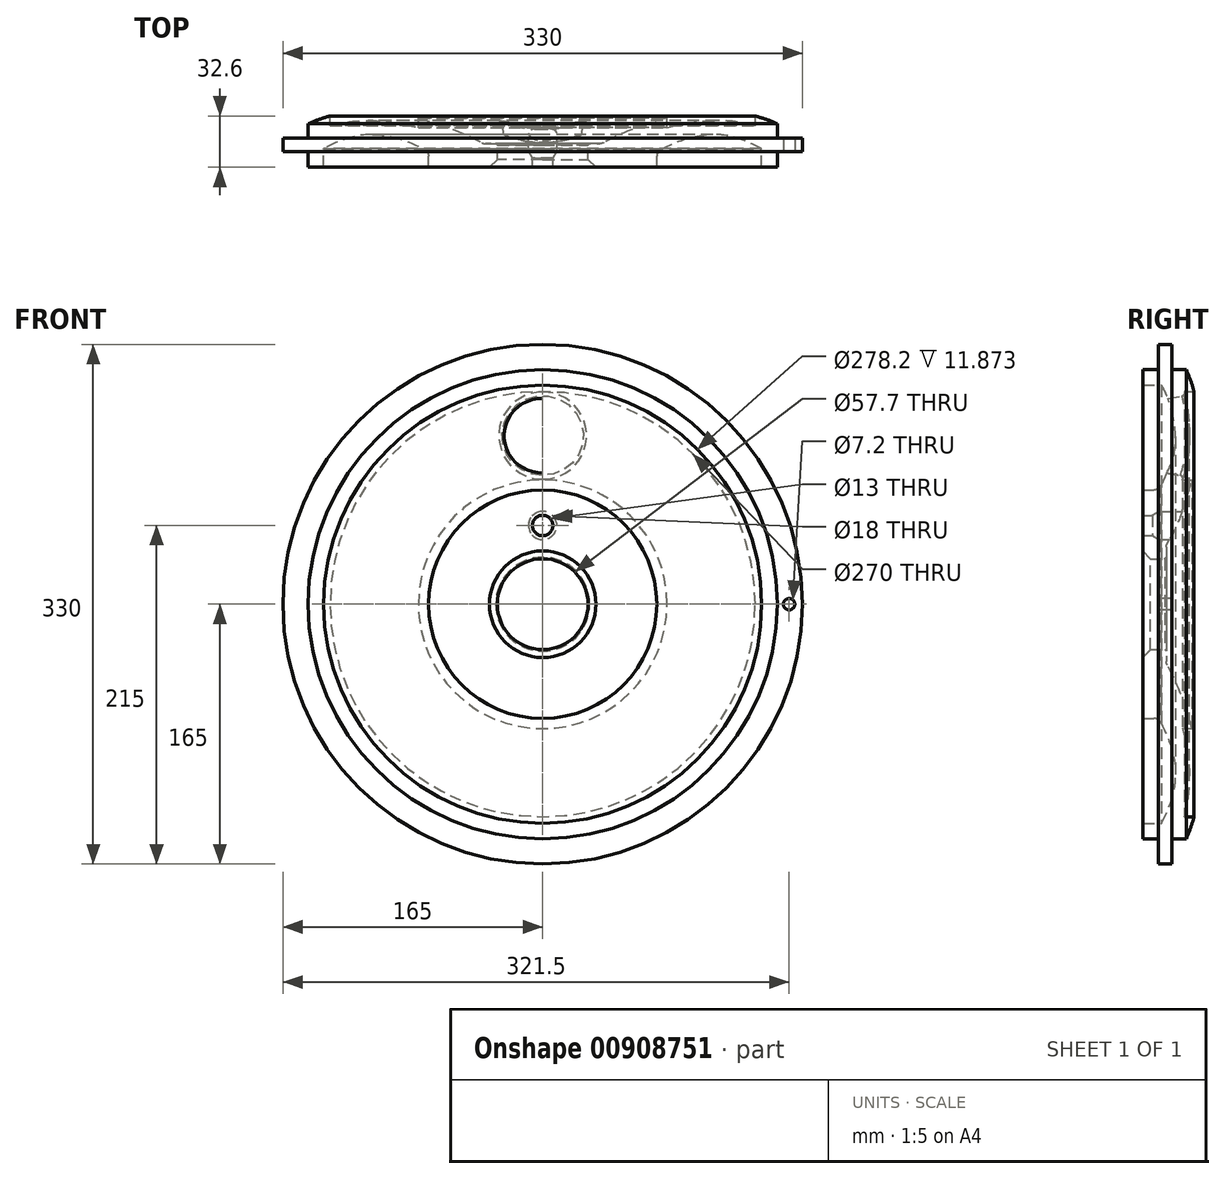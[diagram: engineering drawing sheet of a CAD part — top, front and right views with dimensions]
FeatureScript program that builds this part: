
annotation { "Feature Type Name" : "Feature", "Feature Type Description" : "" }
export const myFeature = defineFeature(function(context is Context, id is Id, definition is map)
    precondition{}
    {
        {
            var Q0;
            Q0=qCreatedBy(makeId("Top.planeOp"),FACE);
            var sketch = newSketch(context, id + "F0", { "sketchPlane" : qUnion([Q0])});
            skLineSegment(sketch, "E0", {"start": v(-28.85, 0) * mm, "end": v(-28.85, 15) * mm});
            skLineSegment(sketch, "E1", {"start": v(-28.85, 15) * mm, "end": v(-36.25, 15) * mm});
            skFitSpline(sketch, "E2", {"points": [v(-37.5, 15) * mm, v(-69.56, 28.6) * mm, v(-105.66, 35.55) * mm, v(-165, 18.67) * mm], "startDerivative": vector(-135.79, 72.9) * mm, "endDerivative": vector(-162.08, -109.99) * mm});
            skLineSegment(sketch, "E3", {"start": v(-165, 10) * mm, "end": v(-149, 10) * mm});
            skLineSegment(sketch, "E4", {"start": v(-149, 10) * mm, "end": v(-149, 0) * mm});
            skLineSegment(sketch, "E5", {"start": v(-149, 0) * mm, "end": v(-139.1, 0) * mm});
            skLineSegment(sketch, "E6", {"start": v(-139.1, 0) * mm, "end": v(-139.1, 11.87) * mm});
            skLineSegment(sketch, "E7", {"start": v(-72.5, 7) * mm, "end": v(-72.5, 0) * mm});
            skLineSegment(sketch, "E8", {"start": v(-72.5, 0) * mm, "end": v(-28.85, 0) * mm});
            skLineSegment(sketch, "E9", {"start": v(0, 47.35) * mm, "end": v(0, -31.33) * mm, "construction": true});
            skFitSpline(sketch, "E10", {"points": [v(-139.1, 11.87) * mm, v(-72.5, 10) * mm], "startDerivative": vector(71.54, 38.93) * mm, "endDerivative": vector(74.78, -40.54) * mm});
            skLineSegment(sketch, "E11", {"start": v(-165, 18.67) * mm, "end": v(-149, 18.67) * mm});
            skLineSegment(sketch, "E12", {"start": v(-149, 18.67) * mm, "end": v(-149, 27.64) * mm});
            skLineSegment(sketch, "E13", {"start": v(-165, 18.67) * mm, "end": v(-165, 10) * mm});
            skArc(sketch, "E14.filletArc", {"start": v(-72.5, 7) * mm, "mid": v(-73.23, 9.6) * mm, "end": v(-75.2, 11.43) * mm});
            skArc(sketch, "E15.filletArc", {"start": v(-38.6, 15.58) * mm, "mid": v(-37.46, 15.15) * mm, "end": v(-36.25, 15) * mm});
            skSolve(sketch);
        }
        {
            var Q0;
            Q0=makeQuery(id+"F0.imprint","IMPRINT",FACE,{"disambiguationData":[TD([[makeQuery(id+"F0.imprint","IMPRINT",EDGE,{"derivedFrom":sQuery(id+"F0.wireOp",EDGE,"E0")}),1.0]])]});
            var Q1;
            Q1=sQuery(id+"F0.wireOp",EDGE,"E9");
            revolve(context, id + "F1", {"surfaceOperationType" : NewSurfaceOperationType.NEW, "entities" : qUnion([Q0]), "axis" : qUnion([Q1]), "revolveType" : RevolveType.FULL});
        }
        {
            var Q0;
            Q0=qCreatedBy(makeId("Front.planeOp"),FACE);
            cPlane(context, id + "F2", {"entities" : qUnion([Q0]), "cplaneType" : CPlaneType.OFFSET, "offset" : 40 * mm, "oppositeDirection" : true, "width" : 150 * mm, "height" : 150 * mm});
        }
        {
            var Q0;
            Q0=qCreatedBy(id+"F2.planeOp",FACE);
            var sketch = newSketch(context, id + "F3", { "sketchPlane" : qUnion([Q0])});
            skPoint(sketch, "E16.visualSharp", {"position": v(0, 43.2) * mm});
            skLineSegment(sketch, "E17", {"start": v(0, 0) * mm, "end": v(0, 148.36) * mm, "construction": true});
            skCircle(sketch, "E18", {"center": v(0, 107) * mm, "radius": 28 * mm});
            skSolve(sketch);
        }
        {
            var Q0;
            Q0=qCreatedBy(makeId("Front.planeOp"),FACE);
            var sketch = newSketch(context, id + "F4", { "sketchPlane" : qUnion([Q0])});
            skCircle(sketch, "E19", {"center": v(156.5, 0) * mm, "radius": 3.6 * mm});
            skSolve(sketch);
        }
        {
            var Q0;
            Q0=qSketchRegion(id+"F4",true);
            extrude(context, id + "F5", {"entities" : qUnion([Q0]), "operationType" : NewBodyOperationType.REMOVE, "oppositeDirection" : true, "depth" : 50 * mm, "offsetDistance" : 25 * mm});
        }
        {
            var Q0;
            Q0=qCreatedBy(makeId("Right.planeOp"),FACE);
            var sketch = newSketch(context, id + "F6", { "sketchPlane" : qUnion([Q0])});
            skLineSegment(sketch, "E20", {"start": v(0, 50) * mm, "end": v(51.06, 50) * mm});
            skLineSegment(sketch, "E21", {"start": v(0, 56.5) * mm, "end": v(6, 56.5) * mm});
            skLineSegment(sketch, "E22", {"start": v(6, 56.5) * mm, "end": v(10.33, 59) * mm});
            skLineSegment(sketch, "E23", {"start": v(10.33, 59) * mm, "end": v(51.06, 59) * mm});
            skLineSegment(sketch, "E24", {"start": v(51.06, 59) * mm, "end": v(51.06, 50) * mm});
            skLineSegment(sketch, "E25", {"start": v(0, 50) * mm, "end": v(0, 56.5) * mm});
            skSolve(sketch);
        }
        {
            var Q0;
            Q0=qSketchRegion(id+"F6",true);
            var Q1;
            Q1=sQuery(id+"F6.wireOp",EDGE,"E20");
            revolve(context, id + "F7", {"operationType" : NewBodyOperationType.REMOVE, "surfaceOperationType" : NewSurfaceOperationType.NEW, "entities" : qUnion([Q0]), "axis" : qUnion([Q1]), "revolveType" : RevolveType.FULL, "oppositeDirection" : true});
        }
        {
            var Q0;
            Q0=makeQuery(id+"F1.opRevolve","SWEPT_EDGE",EDGE,{"disambiguationData":[OSD([sQuery(id+"F0.wireOp",EDGE,"E0"),sQuery(id+"F0.wireOp",EDGE,"E8")])]});
            chamfer(context, id + "F8", {"entities" : qUnion([Q0]), "width" : 5 * mm, "tangentPropagation" : true});
        }
        {
            var Q0;
            Q0=makeQuery(id+"F1.opRevolve","SWEPT_EDGE",EDGE,{"disambiguationData":[OSD([sQuery(id+"F0.wireOp",EDGE,"E0"),sQuery(id+"F0.wireOp",EDGE,"E1")])]});
            chamfer(context, id + "F9", {"entities" : qUnion([Q0]), "width" : 1 * mm, "tangentPropagation" : true});
        }
        {
            var Q0;
            Q0=qSketchRegion(id+"F3",true);
            extrude(context, id + "F10", {"entities" : qUnion([Q0]), "operationType" : NewBodyOperationType.REMOVE, "depth" : 50 * mm, "offsetDistance" : 25 * mm, "hasDraft" : true, "draftAngle" : 10 * degree, "draftPullDirection" : true});
        }
        {
            var Q0;
            Q0=qCreatedBy(id+"F2.planeOp",FACE);
            var sketch = newSketch(context, id + "F11", { "sketchPlane" : qUnion([Q0])});
            skCircle(sketch, "E26", {"center": v(0, 0) * mm, "radius": 135 * mm});
            skCircle(sketch, "E27", {"center": v(0, 0) * mm, "radius": 79 * mm});
            skSolve(sketch);
        }
        {
            var Q0;
            Q0 = qSketchRegion(id + "F11", true);
            var Q1;
            Q1=makeQuery(id+"F1.opRevolve","SWEPT_FACE",FACE,{"disambiguationData":[OSD([sQuery(id+"F0.wireOp",EDGE,"E2")])]});
            extrude(context, id + "F12", {"entities" : qUnion([Q0]), "operationType" : NewBodyOperationType.REMOVE, "endBound" : BoundingType.UP_TO_SURFACE, "depth" : 25 * mm, "endBoundEntityFace" : qUnion([Q1]), "hasOffset" : true, "offsetDistance" : 6 * mm, "offsetOppositeDirection" : true});
        }
        {
            var Q0;
            Q0=makeQuery(id+"F12.boolean.opBoolean","INTERSECT",EDGE,{"derivedFrom":[makeQuery(id+"F10.boolean.opBoolean","COPY",FACE,{"derivedFrom":makeQuery(id+"F10.opExtrude","SWEPT_FACE",FACE,{"disambiguationData":[OSD([sQuery(id+"F3.wireOp",EDGE,"E18")])]})}),makeQuery(id+"F12.opExtrude","CAP_FACE",FACE,{"disambiguationData":[OSD([sQuery(id+"F11.wireOp",EDGE,"E26"),sQuery(id+"F11.wireOp",EDGE,"E27")])],"isStart":false})]});
            var Q1;
            Q1=makeQuery(id+"F12.boolean.opBoolean","INTERSECT",EDGE,{"derivedFrom":[makeQuery(id+"FRi57XyZZzTpHfL_1.11.F10.boolean.opBoolean","COPY",FACE,{"derivedFrom":makeQuery(id+"FRi57XyZZzTpHfL_1.11.F10.opExtrude","SWEPT_FACE",FACE,{"disambiguationData":[OSD([sQuery(id+"F3.wireOp",EDGE,"E18")])]})}),makeQuery(id+"F12.opExtrude","CAP_FACE",FACE,{"disambiguationData":[OSD([sQuery(id+"F11.wireOp",EDGE,"E26"),sQuery(id+"F11.wireOp",EDGE,"E27")])],"isStart":false})]});
            var Q2;
            Q2=makeQuery(id+"F12.boolean.opBoolean","INTERSECT",EDGE,{"derivedFrom":[makeQuery(id+"FRi57XyZZzTpHfL_1.10.F10.boolean.opBoolean","COPY",FACE,{"derivedFrom":makeQuery(id+"FRi57XyZZzTpHfL_1.10.F10.opExtrude","SWEPT_FACE",FACE,{"disambiguationData":[OSD([sQuery(id+"F3.wireOp",EDGE,"E18")])]})}),makeQuery(id+"F12.opExtrude","CAP_FACE",FACE,{"disambiguationData":[OSD([sQuery(id+"F11.wireOp",EDGE,"E26"),sQuery(id+"F11.wireOp",EDGE,"E27")])],"isStart":false})]});
            var Q3;
            Q3=makeQuery(id+"F12.boolean.opBoolean","INTERSECT",EDGE,{"derivedFrom":[makeQuery(id+"FRi57XyZZzTpHfL_1.1.F10.boolean.opBoolean","COPY",FACE,{"derivedFrom":makeQuery(id+"FRi57XyZZzTpHfL_1.1.F10.opExtrude","SWEPT_FACE",FACE,{"disambiguationData":[OSD([sQuery(id+"F3.wireOp",EDGE,"E18")])]})}),makeQuery(id+"F12.opExtrude","CAP_FACE",FACE,{"disambiguationData":[OSD([sQuery(id+"F11.wireOp",EDGE,"E26"),sQuery(id+"F11.wireOp",EDGE,"E27")])],"isStart":false})]});
            var Q4;
            Q4=makeQuery(id+"F12.boolean.opBoolean","INTERSECT",EDGE,{"derivedFrom":[makeQuery(id+"FRi57XyZZzTpHfL_1.2.F10.boolean.opBoolean","COPY",FACE,{"derivedFrom":makeQuery(id+"FRi57XyZZzTpHfL_1.2.F10.opExtrude","SWEPT_FACE",FACE,{"disambiguationData":[OSD([sQuery(id+"F3.wireOp",EDGE,"E18")])]})}),makeQuery(id+"F12.opExtrude","CAP_FACE",FACE,{"disambiguationData":[OSD([sQuery(id+"F11.wireOp",EDGE,"E26"),sQuery(id+"F11.wireOp",EDGE,"E27")])],"isStart":false})]});
            var Q5;
            Q5=makeQuery(id+"F12.boolean.opBoolean","INTERSECT",EDGE,{"derivedFrom":[makeQuery(id+"FRi57XyZZzTpHfL_1.3.F10.boolean.opBoolean","COPY",FACE,{"derivedFrom":makeQuery(id+"FRi57XyZZzTpHfL_1.3.F10.opExtrude","SWEPT_FACE",FACE,{"disambiguationData":[OSD([sQuery(id+"F3.wireOp",EDGE,"E18")])]})}),makeQuery(id+"F12.opExtrude","CAP_FACE",FACE,{"disambiguationData":[OSD([sQuery(id+"F11.wireOp",EDGE,"E26"),sQuery(id+"F11.wireOp",EDGE,"E27")])],"isStart":false})]});
            var Q6;
            Q6=makeQuery(id+"F12.boolean.opBoolean","INTERSECT",EDGE,{"derivedFrom":[makeQuery(id+"FRi57XyZZzTpHfL_1.4.F10.boolean.opBoolean","COPY",FACE,{"derivedFrom":makeQuery(id+"FRi57XyZZzTpHfL_1.4.F10.opExtrude","SWEPT_FACE",FACE,{"disambiguationData":[OSD([sQuery(id+"F3.wireOp",EDGE,"E18")])]})}),makeQuery(id+"F12.opExtrude","CAP_FACE",FACE,{"disambiguationData":[OSD([sQuery(id+"F11.wireOp",EDGE,"E26"),sQuery(id+"F11.wireOp",EDGE,"E27")])],"isStart":false})]});
            var Q7;
            Q7=makeQuery(id+"F12.boolean.opBoolean","INTERSECT",EDGE,{"derivedFrom":[makeQuery(id+"FRi57XyZZzTpHfL_1.5.F10.boolean.opBoolean","COPY",FACE,{"derivedFrom":makeQuery(id+"FRi57XyZZzTpHfL_1.5.F10.opExtrude","SWEPT_FACE",FACE,{"disambiguationData":[OSD([sQuery(id+"F3.wireOp",EDGE,"E18")])]})}),makeQuery(id+"F12.opExtrude","CAP_FACE",FACE,{"disambiguationData":[OSD([sQuery(id+"F11.wireOp",EDGE,"E26"),sQuery(id+"F11.wireOp",EDGE,"E27")])],"isStart":false})]});
            var Q8;
            Q8=makeQuery(id+"F12.boolean.opBoolean","INTERSECT",EDGE,{"derivedFrom":[makeQuery(id+"FRi57XyZZzTpHfL_1.6.F10.boolean.opBoolean","COPY",FACE,{"derivedFrom":makeQuery(id+"FRi57XyZZzTpHfL_1.6.F10.opExtrude","SWEPT_FACE",FACE,{"disambiguationData":[OSD([sQuery(id+"F3.wireOp",EDGE,"E18")])]})}),makeQuery(id+"F12.opExtrude","CAP_FACE",FACE,{"disambiguationData":[OSD([sQuery(id+"F11.wireOp",EDGE,"E26"),sQuery(id+"F11.wireOp",EDGE,"E27")])],"isStart":false})]});
            var Q9;
            Q9=makeQuery(id+"F12.boolean.opBoolean","INTERSECT",EDGE,{"derivedFrom":[makeQuery(id+"FRi57XyZZzTpHfL_1.7.F10.boolean.opBoolean","COPY",FACE,{"derivedFrom":makeQuery(id+"FRi57XyZZzTpHfL_1.7.F10.opExtrude","SWEPT_FACE",FACE,{"disambiguationData":[OSD([sQuery(id+"F3.wireOp",EDGE,"E18")])]})}),makeQuery(id+"F12.opExtrude","CAP_FACE",FACE,{"disambiguationData":[OSD([sQuery(id+"F11.wireOp",EDGE,"E26"),sQuery(id+"F11.wireOp",EDGE,"E27")])],"isStart":false})]});
            var Q10;
            Q10=makeQuery(id+"F12.boolean.opBoolean","INTERSECT",EDGE,{"derivedFrom":[makeQuery(id+"FRi57XyZZzTpHfL_1.8.F10.boolean.opBoolean","COPY",FACE,{"derivedFrom":makeQuery(id+"FRi57XyZZzTpHfL_1.8.F10.opExtrude","SWEPT_FACE",FACE,{"disambiguationData":[OSD([sQuery(id+"F3.wireOp",EDGE,"E18")])]})}),makeQuery(id+"F12.opExtrude","CAP_FACE",FACE,{"disambiguationData":[OSD([sQuery(id+"F11.wireOp",EDGE,"E26"),sQuery(id+"F11.wireOp",EDGE,"E27")])],"isStart":false})]});
            var Q11;
            Q11=makeQuery(id+"F12.boolean.opBoolean","INTERSECT",EDGE,{"derivedFrom":[makeQuery(id+"FRi57XyZZzTpHfL_1.9.F10.boolean.opBoolean","COPY",FACE,{"derivedFrom":makeQuery(id+"FRi57XyZZzTpHfL_1.9.F10.opExtrude","SWEPT_FACE",FACE,{"disambiguationData":[OSD([sQuery(id+"F3.wireOp",EDGE,"E18")])]})}),makeQuery(id+"F12.opExtrude","CAP_FACE",FACE,{"disambiguationData":[OSD([sQuery(id+"F11.wireOp",EDGE,"E26"),sQuery(id+"F11.wireOp",EDGE,"E27")])],"isStart":false})]});
            fillet(context, id + "F13", {"entities" : qUnion([Q0, Q1, Q2, Q3, Q4, Q5, Q6, Q7, Q8, Q9, Q10, Q11]), "radius" : 2 * mm, "tangentPropagation" : true, "allowEdgeOverflow" : false});
        }
    });
